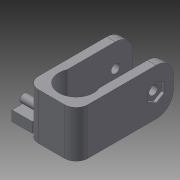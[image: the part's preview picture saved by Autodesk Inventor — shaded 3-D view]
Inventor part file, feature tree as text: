
AUTODESK INVENTOR PART (.ipt)
format: ipt  version: 2015 SP1 (Build 190203100, 203)  size: 218,624 bytes
history: native  units: mm
features: extrude x6, sketch x6, projected_geometry x5, fillet x2, hole x1
ambient origin geometry x8: Origin, YZ Plane, XZ Plane, XY Plane, X Axis, Y Axis, Z Axis, Center Point
bodies: Solid1 (feature_tree)
feature tree (20):
  extrude  "Extrusion1"  Depth=3.0mm
  fillet  "Fillet1"  Radius=3.0mm
  extrude  "Extrusion2"  Depth=8.5mm
  extrude  "Extrusion3"  Depth=6.0mm
  fillet  "Fillet2"  Radius=2.8mm
  hole  "Hole1"  [1 undecoded]
  extrude  "Extrusion4"  Depth=6.0mm
  extrude  "Extrusion6"  Depth=7.0mm TaperAngle=0.0deg
  extrude  "Extrusion7"  Depth=4.0mm
  sketch  "Sketch1"  dims[d0=12.0mm d2=25.0mm d4=3.0mm]
  sketch  "Sketch2"  dims[d5=3.0mm d6=8.5mm]
  sketch  "Sketch3"  dims[d7=16.0mm d8=0.0mm d9=6.0mm d10=2.8mm]
  projected_geometry  "Projected Loop1"
  sketch  "Sketch5"  dims[d11=2.8mm d12=9.525mm]
  projected_geometry  "Projected Loop2"
  sketch  "Sketch6"  dims[d13=5.0mm d14=6.0mm]
  projected_geometry  "Projected Loop3"
  projected_geometry  "Projected Loop4"
  projected_geometry  "Projected Loop5"
  sketch  "Sketch7"  dims[d15=7.0mm d16=0.0mm d17=7.0mm d18=0.0mm d19=4.0mm d20=6.0mm d21=8.0mm d22=3.0mm d23=6.0mm d24=4.0mm d25=2.0mm d26=90.0deg d27=8.0mm d28=20.594885mm d29=5.6mm d30=1.0mm d31=0.0mm d34=3.5mm d35=0.0mm d36=0.5mm d37=0.0mm]
note: 1 required parameter value undecoded (feature->parameter linkage not recoverable at this tier; creation-order binding heuristic only, values carry confidence <= 0.55)
